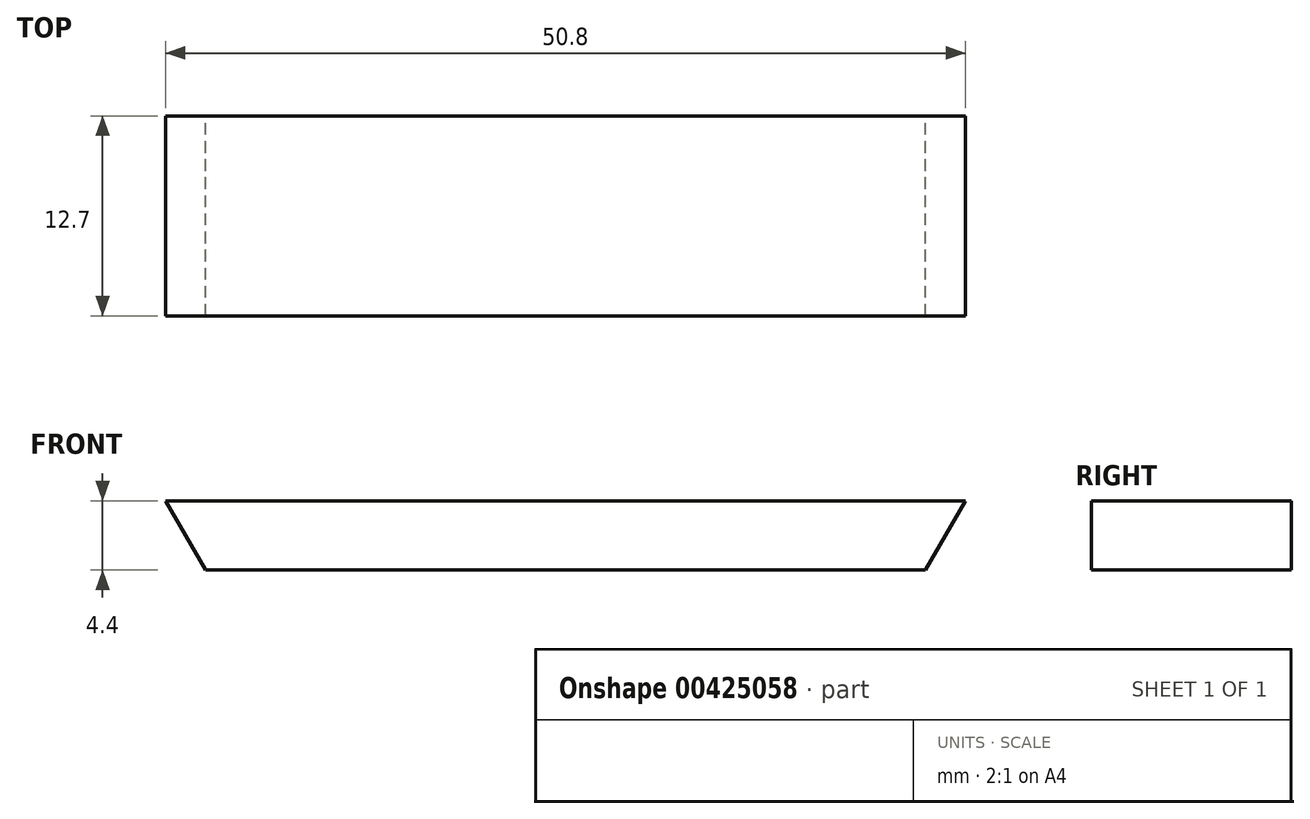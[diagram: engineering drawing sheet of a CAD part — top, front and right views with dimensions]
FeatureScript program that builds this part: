
annotation { "Feature Type Name" : "Feature", "Feature Type Description" : "" }
export const myFeature = defineFeature(function(context is Context, id is Id, definition is map)
    precondition{}
    {
        {
            var Q0;
            Q0=qCreatedBy(makeId("Front.planeOp"),FACE);
            var sketch = newSketch(context, id + "F0", { "sketchPlane" : qUnion([Q0])});
            skLineSegment(sketch, "E0", {"start": v(-14.91, 52.3) * mm, "end": v(-12.37, 47.9) * mm});
            skLineSegment(sketch, "E1", {"start": v(-12.37, 47.9) * mm, "end": v(33.35, 47.9) * mm});
            skLineSegment(sketch, "E2", {"start": v(33.35, 47.9) * mm, "end": v(35.89, 52.3) * mm});
            skLineSegment(sketch, "E3", {"start": v(35.89, 52.3) * mm, "end": v(-14.91, 52.3) * mm});
            skSolve(sketch);
        }
        {
            var Q0;
            Q0 = qSketchRegion(id + "F0", true);
            extrude(context, id + "F1", {"entities" : qUnion([Q0]), "depth" : 12.7 * mm});
        }
    });
